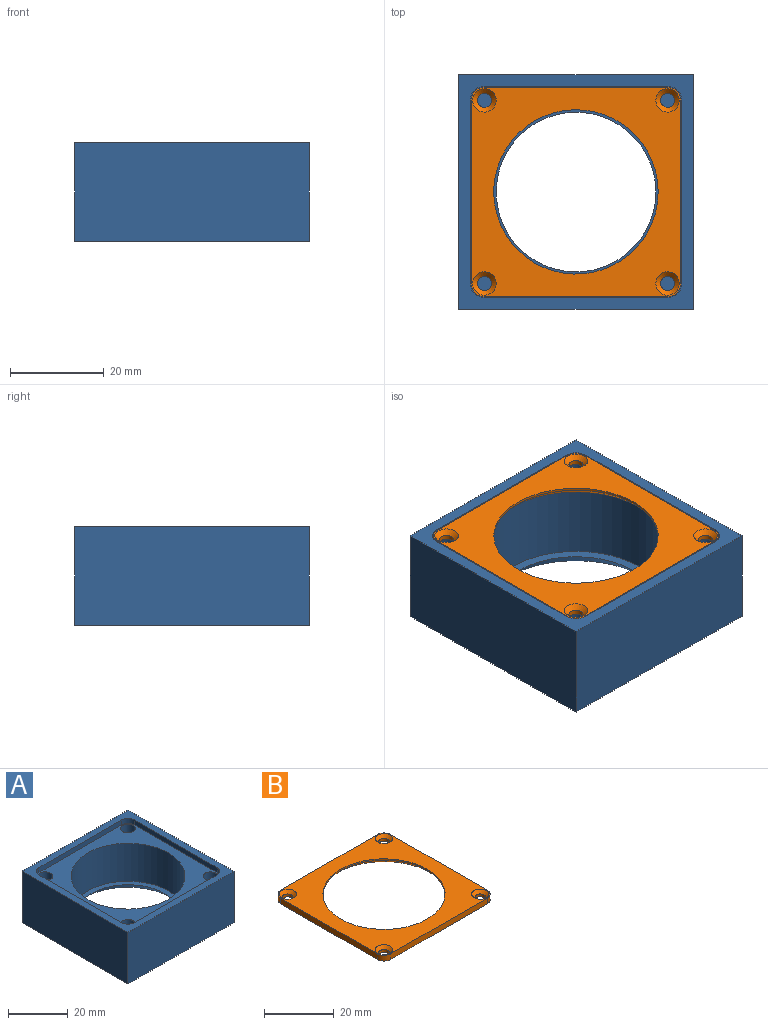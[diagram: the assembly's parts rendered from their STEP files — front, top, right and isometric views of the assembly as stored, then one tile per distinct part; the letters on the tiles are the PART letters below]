
ASSEMBLY  parts=2 mates=1
PART A: 26 faces, bbox 50x50x21 mm
  f0: cylinder r=19mm len=38mm, axis (0,0,1), area 1850.4mm2, adj f8,f17
  f1: plane 50x21mm, normal (0,-1,0), area 1050mm2, adj f2,f4,f5,f6
  f2: plane 50x21mm, normal (1,0,0), area 1050mm2, adj f1,f3,f5,f6
  f3: plane 50x21mm, normal (0,1,0), area 1050mm2, adj f2,f4,f5,f6
  f4: plane 50x21mm, normal (-1,0,0), area 1050mm2, adj f1,f3,f5,f6
  f5: plane 50x50mm, normal (0,0,1), area 482.7mm2, adj f1,f2,f3,f4,f9,f10,f11,f12
  f6: plane 50x50mm, normal (0,0,-1), area 1179.7mm2, adj f1,f2,f3,f4,f7
  f7: cone r=20.5mm half-angle=45deg, axis (0,0,-1), area 583.1mm2, adj f6,f8
  f8: plane 38x38mm, normal (0,0,1), area 226.2mm2, adj f0,f7
  f9: cylinder r=3mm len=3mm, axis (0,0,1), area 9.4mm2, adj f5,f10,f16,f17
  f10: plane 39x2mm, normal (0,1,0), area 78mm2, adj f5,f9,f11,f17
  f11: cylinder r=3mm len=3mm, axis (0,0,1), area 9.4mm2, adj f5,f10,f12,f17
  f12: plane 39x2mm, normal (-1,0,0), area 78mm2, adj f5,f11,f13,f17
  f13: cylinder r=3mm len=3mm, axis (0,0,1), area 9.4mm2, adj f5,f12,f14,f17
  f14: plane 39x2mm, normal (0,-1,0), area 78mm2, adj f5,f13,f15,f17
  f15: cylinder r=3mm len=3mm, axis (0,0,1), area 9.4mm2, adj f5,f14,f16,f17
  f16: plane 39x2mm, normal (1,0,0), area 78mm2, adj f5,f9,f15,f17
  f17: plane 45x45mm, normal (0,0,1), area 804.6mm2, adj f0,f9,f10,f11,f12,f13,f14,f15
  f18: cylinder r=2.5mm len=10mm, axis (0,0,1), area 157.1mm2, adj f17,f19
  f19: plane 5x5mm, normal (0,0,1), area 19.6mm2, adj f18
  f20: cylinder r=2.5mm len=10mm, axis (0,0,1), area 157.1mm2, adj f17,f21
  f21: plane 5x5mm, normal (0,0,1), area 19.6mm2, adj f20
  f22: cylinder r=2.5mm len=10mm, axis (0,0,1), area 157.1mm2, adj f17,f23
  f23: plane 5x5mm, normal (0,0,1), area 19.6mm2, adj f22
  f24: cylinder r=2.5mm len=10mm, axis (0,0,1), area 157.1mm2, adj f17,f25
  f25: plane 5x5mm, normal (0,0,1), area 19.6mm2, adj f24
PART B: 20 faces, bbox 44.6x44.6x2 mm
  f0: plane 39x2mm, normal (-1,0,0), area 78mm2, adj f1,f12,f13,f14
  f1: cylinder r=2.8mm len=2.8mm, axis (0,0,-1), area 8.8mm2, adj f0,f2,f13,f14
  f2: plane 39x2mm, normal (0,-1,0), area 78mm2, adj f1,f3,f13,f14
  f3: cylinder r=2.8mm len=2.8mm, axis (0,0,-1), area 8.8mm2, adj f2,f4,f13,f14
  f4: plane 39x2mm, normal (1,0,0), area 78mm2, adj f3,f5,f13,f14
  f5: cylinder r=2.8mm len=2.8mm, axis (0,0,-1), area 8.8mm2, adj f4,f6,f13,f14
  f6: plane 39x2mm, normal (0,1,0), area 78mm2, adj f5,f12,f13,f14
  f7: cylinder r=1.5mm len=3mm, axis (0,0,-1), area 9.4mm2, adj f14,f18
  f8: cylinder r=1.5mm len=3mm, axis (0,0,-1), area 9.4mm2, adj f14,f17
  f9: cylinder r=1.5mm len=3mm, axis (0,0,-1), area 9.4mm2, adj f14,f16
  f10: cylinder r=1.5mm len=3mm, axis (0,0,-1), area 9.4mm2, adj f14,f15
  f11: cylinder r=17.5mm len=35mm, axis (0,0,-1), area 55mm2, adj f13,f19
  f12: cylinder r=2.8mm len=2.8mm, axis (0,0,-1), area 8.8mm2, adj f0,f6,f13,f14
  f13: plane 44.6x44.6mm, normal (0,0,1), area 941.8mm2, adj f0,f1,f2,f3,f4,f5,f6,f11
  f14: plane 44.6x44.6mm, normal (0,0,-1), area 820mm2, adj f0,f1,f2,f3,f4,f5,f6,f7
  f15: cone r=1.5mm half-angle=45deg, axis (0,0,1), area 17.8mm2, adj f10,f13
  f16: cone r=1.5mm half-angle=45deg, axis (0,0,1), area 17.8mm2, adj f9,f13
  f17: cone r=1.5mm half-angle=45deg, axis (0,0,1), area 17.8mm2, adj f8,f13
  f18: cone r=1.5mm half-angle=45deg, axis (0,0,1), area 17.8mm2, adj f7,f13
  f19: cone r=19mm half-angle=45deg, axis (0,0,-1), area 243.2mm2, adj f11,f14
PLACE A at identity
PLACE B t=(0,0,19)mm
MATE fastened B.f11 <-> A.f7  axis (0,0,-1) through (0,0,19)mm
